# Revit family: Gira_537702
name_source: partatom
category: Electrical Fixtures
revit_build: Autodesk Revit 2017 (Build: 20160225_1515(x64)
units: mm (PartAtom-declared; Revit-internal decimal feet)

## family parameters
Cut with Voids When Loaded = No
Host = Face
Maintain Annotation Orientation = Yes
Part Type = Normal
Room Calculation Point = No
Round Connector Dimension = Use Diameter
Shared = No

## types (1)
- S3000 Präsenz- + Beweg.m. 360°-Aufs. BT Wächter
    Abdimmfunktion mit Dimmeinsatz = Yes
    Alarmfunktion = No
    Anschlussart = sonstige
    Ansprechempfindlichkeit einstellbar = Yes
    Ansprechhelligkeit einstellbar = Yes
    Antibakterielle Behandlung = No
    Ausführung = Präsenzmelder
    Available = Yes
    Category = Bewegungsmelder komplett
    Data sheet (1) = https://katalog.gira.de
    Default Elevation = 1219 mm
    Farbe = weiß
    Fernbedienbar = Yes
    GTIN = 4010337052227
    Geeignet für C-Last = No
    Geeignet für Deckenmontage = Yes
    Geeignet für Wandmontage = Yes
    Geeignet für drahtlose Übertragung = No
    HAN = 537702
    HLK-Ansteuerung = No
    Halogenfrei = Yes
    HeinzeBIM = https://bimportal.heinze.de
    Keynote = Bewegungsmelder_360°-Aufsatz
    Konstantlichtregelung = Yes
    Manufacturer URL = https://www.gira.de
    Mit DALI-Schnittstelle = No
    Mit Fernbedienung = No
    Mit Signaleinheit = No
    Montageart = sonstige
    Name = S3000 Präsenz- + Beweg.m. 360°-Aufs. BT Wächter
    Nebenstelleneingang = Yes
    Oberfläche = sonstige
    Region = DE
    Scanwinkel = 360 °
    Sensortyp = passiv Infrarot
    Teach-Funktion für Ansprechhelligkeit = No
    Tierschneise = No
    Transparent = No
    Treppenhausüberwachung = No
    URL = http://katalog.gira.de
    Unterkriechschutz/Rückfeldüberwachung = No
    Vernetzbar = No
    Werkstoff = sonstige
    Werkstoffgüte = sonstige
    Zwangsabschaltung = No
    Zwangseinschaltung = No
    Überbrückungsschalter = No

## geometry (parser evidence)
native form markers: Blend x2, Sweep x3
no freeform markers — native parametric forms only
